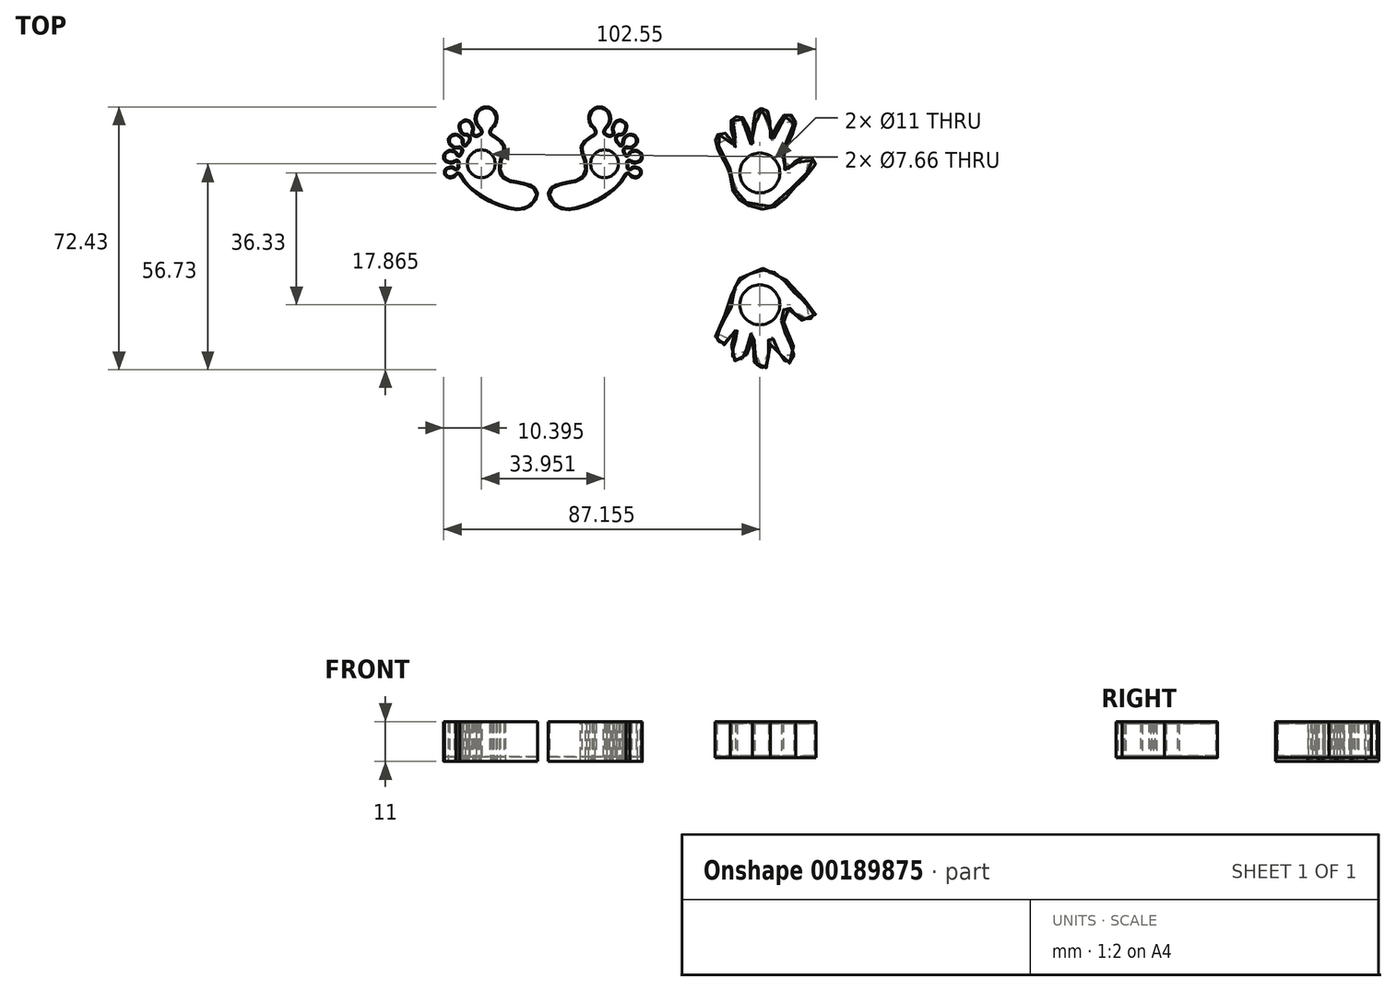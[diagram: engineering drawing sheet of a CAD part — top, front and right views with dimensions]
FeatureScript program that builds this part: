
annotation { "Feature Type Name" : "Feature", "Feature Type Description" : "" }
export const myFeature = defineFeature(function(context is Context, id is Id, definition is map)
    precondition{}
    {
        {
            var Q0;
            Q0=qCreatedBy(makeId("Top.planeOp"),FACE);
            var sketch = newSketch(context, id + "F0", { "sketchPlane" : qUnion([Q0])});
            skFitSpline(sketch, "E0", {"points": [v(-38.1, 15.91) * mm, v(-41.17, 17.42) * mm, v(-41.33, 22.02) * mm, v(-40.43, 25.18) * mm, v(-43.51, 28.42) * mm, v(-47.73, 28.72) * mm, v(-51.85, 25.13) * mm, v(-53.32, 19) * mm, v(-49.92, 13.8) * mm, v(-44.12, 10.03) * mm, v(-37.56, 8.03) * mm, v(-33.86, 8.82) * mm, v(-31.52, 11.84) * mm, v(-32.2, 13.95) * mm, v(-34.84, 15.23) * mm, v(-38.1, 15.91) * mm]});
            skFitSpline(sketch, "E1", {"points": [v(-45.64, 29.93) * mm, v(-43.87, 30.6) * mm, v(-42.7, 32.44) * mm, v(-43.04, 34.88) * mm, v(-44.75, 36.27) * mm, v(-46.72, 36.18) * mm, v(-48.3, 34.75) * mm, v(-48.65, 32.6) * mm, v(-47.95, 31) * mm, v(-46.78, 30.06) * mm, v(-45.64, 29.93) * mm]});
            skFitSpline(sketch, "E2", {"points": [v(-49.41, 31.45) * mm, v(-49.98, 32.28) * mm, v(-50.87, 32.78) * mm, v(-52.04, 32.53) * mm, v(-53.03, 31.7) * mm, v(-53.06, 30.34) * mm, v(-52.61, 29.27) * mm, v(-51.97, 28.76) * mm, v(-50.65, 28.57) * mm, v(-49.57, 29.17) * mm, v(-49.03, 30.34) * mm, v(-49.41, 31.45) * mm]});
            skFitSpline(sketch, "E3", {"points": [v(-51.97, 27.04) * mm, v(-52.6, 28.18) * mm, v(-53.97, 28.89) * mm, v(-55.6, 28.32) * mm, v(-56.07, 27.05) * mm, v(-55.62, 25.97) * mm, v(-54.67, 25.18) * mm, v(-53.54, 24.99) * mm, v(-52.33, 25.56) * mm, v(-51.97, 27.04) * mm]});
            skPoint(sketch, "E4.4.internal.snap0", {"position": v(-57.36, 23.03) * mm});
            skFitSpline(sketch, "E4", {"points": [v(-57.36, 22.44) * mm, v(-57.08, 23.61) * mm, v(-55.76, 24.4) * mm, v(-54.02, 24.04) * mm, v(-53.54, 23.03) * mm, v(-54.02, 21.44) * mm, v(-55.3, 20.87) * mm, v(-56.48, 21.16) * mm, v(-57.09, 21.62) * mm, v(-57.36, 22.44) * mm]});
            skFitSpline(sketch, "E5", {"points": [v(-54.25, 19.45) * mm, v(-53.88, 19.13) * mm, v(-53.66, 18.32) * mm, v(-54.2, 17.29) * mm, v(-55.58, 16.82) * mm, v(-56.56, 17.2) * mm, v(-57.15, 18.02) * mm, v(-56.88, 19.21) * mm, v(-55.9, 19.75) * mm, v(-54.82, 19.77) * mm, v(-54.25, 19.45) * mm]});
            skFitSpline(sketch, "E6", {"points": [v(-43.51, 28.42) * mm, v(-44.4, 29.3) * mm, v(-43.87, 30.6) * mm], "startDerivative": vector(-2.53, 1.63) * mm, "endDerivative": vector(1.79, 2.7) * mm});
            skFitSpline(sketch, "E7", {"points": [v(-47.73, 28.72) * mm, v(-47, 29.35) * mm, v(-47.41, 30.46) * mm], "startDerivative": vector(2.09, 1.14) * mm, "endDerivative": vector(-1.38, 2.3) * mm});
            skFitSpline(sketch, "E8", {"points": [v(-48.22, 28.52) * mm, v(-49.15, 28.79) * mm, v(-49.22, 29.66) * mm], "startDerivative": vector(-2.81, -0.03) * mm, "endDerivative": vector(0.87, 2.36) * mm});
            skFitSpline(sketch, "E9", {"points": [v(-50.47, 26.88) * mm, v(-50.35, 28.04) * mm, v(-50.96, 28.55) * mm], "startDerivative": vector(1.15, 2.94) * mm, "endDerivative": vector(-2.3, 0.33) * mm});
            skFitSpline(sketch, "E10", {"points": [v(-51.28, 25.94) * mm, v(-51.74, 25.98) * mm, v(-51.96, 26.57) * mm], "startDerivative": vector(-1.33, -0.55) * mm, "endDerivative": vector(-0.3, 1.2) * mm});
            skFitSpline(sketch, "E11", {"points": [v(-52.37, 24.2) * mm, v(-52.56, 24.84) * mm, v(-53.07, 25.08) * mm], "startDerivative": vector(0.03, 1.48) * mm, "endDerivative": vector(-1.63, 0.12) * mm});
            skFitSpline(sketch, "E12", {"points": [v(-52.74, 23.38) * mm, v(-53.1, 23.03) * mm, v(-53.61, 23.47) * mm], "startDerivative": vector(-0.84, -1.47) * mm, "endDerivative": vector(-0.87, 1.67) * mm});
            skFitSpline(sketch, "E13", {"points": [v(-53.38, 20.87) * mm, v(-53.54, 21.35) * mm, v(-54.25, 21.22) * mm], "startDerivative": vector(0.22, 1.99) * mm, "endDerivative": vector(-1.97, -1.2) * mm});
            skFitSpline(sketch, "E14", {"points": [v(-52.87, 17.57) * mm, v(-53.3, 17.9) * mm, v(-53.9, 17.63) * mm], "startDerivative": vector(-0.86, 1) * mm, "endDerivative": vector(-1.18, -0.85) * mm});
            skFitSpline(sketch, "E15", {"points": [v(-53.41, 19.75) * mm, v(-53.66, 19.44) * mm, v(-54.16, 19.39) * mm], "startDerivative": vector(-0.37, -1.42) * mm, "endDerivative": vector(-1.16, 0.72) * mm});
            skSolve(sketch);
        }
        {
            var Q0;
            Q0 = qSketchRegion(id + "F0", true);
            extrude(context, id + "F1", {"entities" : qUnion([Q0]), "depth" : 10 * mm});
        }
        {
            var Q0;
            Q0=makeQuery(id+"F1.opExtrude","CAP_FACE",FACE,{"disambiguationData":[OSD([sQuery(id+"F0.wireOp",EDGE,"E0"),sQuery(id+"F0.wireOp",EDGE,"E1"),sQuery(id+"F0.wireOp",EDGE,"E2"),sQuery(id+"F0.wireOp",EDGE,"E3"),sQuery(id+"F0.wireOp",EDGE,"E4"),sQuery(id+"F0.wireOp",EDGE,"E5"),sQuery(id+"F0.wireOp",EDGE,"E6"),sQuery(id+"F0.wireOp",EDGE,"E7"),sQuery(id+"F0.wireOp",EDGE,"E8"),sQuery(id+"F0.wireOp",EDGE,"E9"),sQuery(id+"F0.wireOp",EDGE,"E0"),sQuery(id+"F0.wireOp",EDGE,"E10"),sQuery(id+"F0.wireOp",EDGE,"E11"),sQuery(id+"F0.wireOp",EDGE,"E12"),sQuery(id+"F0.wireOp",EDGE,"E13"),sQuery(id+"F0.wireOp",EDGE,"E14"),sQuery(id+"F0.wireOp",EDGE,"E15"),sQuery(id+"F0.wireOp",EDGE,"E0"),sQuery(id+"F0.wireOp",EDGE,"E0"),sQuery(id+"F0.wireOp",EDGE,"E0")])],"isStart":false});
            shell(context, id + "F2", {"entities" : qUnion([Q0]), "thickness" : .3 * mm});
        }
        {
            var Q0;
            {var subQ0=sQuery(id+"F0.wireOp",EDGE,"E1");Q0=makeQuery(id+"F2.opShell","OFFSET_EDGE",EDGE,{"disambiguationData":[OSD([subQ0]),TDD([makeQuery(id+"F1.opExtrude","CAP_EDGE",EDGE,{"disambiguationData":[OSD([subQ0])],"isStart":false})])]});}
            var Q1;
            {var subQ0=sQuery(id+"F0.wireOp",EDGE,"E2");Q1=makeQuery(id+"F2.opShell","OFFSET_EDGE",EDGE,{"disambiguationData":[OSD([subQ0]),TDD([makeQuery(id+"F1.opExtrude","CAP_EDGE",EDGE,{"disambiguationData":[OSD([subQ0])],"isStart":false})])]});}
            var Q2;
            {var subQ0=sQuery(id+"F0.wireOp",EDGE,"E3");Q2=makeQuery(id+"F2.opShell","OFFSET_EDGE",EDGE,{"disambiguationData":[OSD([subQ0]),TDD([makeQuery(id+"F1.opExtrude","CAP_EDGE",EDGE,{"disambiguationData":[OSD([subQ0])],"isStart":false})])]});}
            var Q3;
            {var subQ0=sQuery(id+"F0.wireOp",EDGE,"E4");Q3=makeQuery(id+"F2.opShell","OFFSET_EDGE",EDGE,{"disambiguationData":[OSD([subQ0]),TDD([makeQuery(id+"F1.opExtrude","CAP_EDGE",EDGE,{"disambiguationData":[OSD([subQ0])],"isStart":false})])]});}
            var Q4;
            {var subQ0=sQuery(id+"F0.wireOp",EDGE,"E5");Q4=makeQuery(id+"F2.opShell","OFFSET_EDGE",EDGE,{"disambiguationData":[OSD([subQ0]),TDD([makeQuery(id+"F1.opExtrude","CAP_EDGE",EDGE,{"disambiguationData":[OSD([subQ0])],"isStart":false})])]});}
            var Q5;
            {var subQ0=sQuery(id+"F0.wireOp",EDGE,"E7");Q5=makeQuery(id+"F2.opShell","OFFSET_EDGE",EDGE,{"disambiguationData":[OSD([subQ0]),TDD([makeQuery(id+"F1.opExtrude","CAP_EDGE",EDGE,{"disambiguationData":[OSD([subQ0])],"isStart":false})])]});}
            var Q6;
            {var subQ0=sQuery(id+"F0.wireOp",EDGE,"E8");Q6=makeQuery(id+"F2.opShell","OFFSET_EDGE",EDGE,{"disambiguationData":[OSD([subQ0]),TDD([makeQuery(id+"F1.opExtrude","CAP_EDGE",EDGE,{"disambiguationData":[OSD([subQ0])],"isStart":false})])]});}
            var Q7;
            {var subQ0=sQuery(id+"F0.wireOp",EDGE,"E9");Q7=makeQuery(id+"F2.opShell","OFFSET_EDGE",EDGE,{"disambiguationData":[OSD([subQ0]),TDD([makeQuery(id+"F1.opExtrude","CAP_EDGE",EDGE,{"disambiguationData":[OSD([subQ0])],"isStart":false})])]});}
            var Q8;
            {var subQ0=sQuery(id+"F0.wireOp",EDGE,"E10");Q8=makeQuery(id+"F2.opShell","OFFSET_EDGE",EDGE,{"disambiguationData":[OSD([subQ0]),TDD([makeQuery(id+"F1.opExtrude","CAP_EDGE",EDGE,{"disambiguationData":[OSD([subQ0])],"isStart":false})])]});}
            var Q9;
            {var subQ0=sQuery(id+"F0.wireOp",EDGE,"E11");Q9=makeQuery(id+"F2.opShell","OFFSET_EDGE",EDGE,{"disambiguationData":[OSD([subQ0]),TDD([makeQuery(id+"F1.opExtrude","CAP_EDGE",EDGE,{"disambiguationData":[OSD([subQ0])],"isStart":false})])]});}
            var Q10;
            {var subQ0=sQuery(id+"F0.wireOp",EDGE,"E12");Q10=makeQuery(id+"F2.opShell","OFFSET_EDGE",EDGE,{"disambiguationData":[OSD([subQ0]),TDD([makeQuery(id+"F1.opExtrude","CAP_EDGE",EDGE,{"disambiguationData":[OSD([subQ0])],"isStart":false})])]});}
            var Q11;
            {var subQ0=sQuery(id+"F0.wireOp",EDGE,"E13");Q11=makeQuery(id+"F2.opShell","OFFSET_EDGE",EDGE,{"disambiguationData":[OSD([subQ0]),TDD([makeQuery(id+"F1.opExtrude","CAP_EDGE",EDGE,{"disambiguationData":[OSD([subQ0])],"isStart":false})])]});}
            var Q12;
            {var subQ0=sQuery(id+"F0.wireOp",EDGE,"E15");Q12=makeQuery(id+"F2.opShell","OFFSET_EDGE",EDGE,{"disambiguationData":[OSD([subQ0]),TDD([makeQuery(id+"F1.opExtrude","CAP_EDGE",EDGE,{"disambiguationData":[OSD([subQ0])],"isStart":false})])]});}
            var Q13;
            {var subQ0=sQuery(id+"F0.wireOp",EDGE,"E14");Q13=makeQuery(id+"F2.opShell","OFFSET_EDGE",EDGE,{"disambiguationData":[OSD([subQ0]),TDD([makeQuery(id+"F1.opExtrude","CAP_EDGE",EDGE,{"disambiguationData":[OSD([subQ0])],"isStart":false})])]});}
            var Q14;
            {var subQ0=sQuery(id+"F0.wireOp",EDGE,"E0");Q14=makeQuery(id+"F2.opShell","OFFSET_EDGE",EDGE,{"disambiguationData":[OSD([subQ0]),TDD([makeQuery(id+"F1.opExtrude","CAP_EDGE",EDGE,{"disambiguationData":[OSD([subQ0])],"isStart":false})])]});}
            var Q15;
            {var subQ0=sQuery(id+"F0.wireOp",EDGE,"E6");Q15=makeQuery(id+"F2.opShell","OFFSET_EDGE",EDGE,{"disambiguationData":[OSD([subQ0]),TDD([makeQuery(id+"F1.opExtrude","CAP_EDGE",EDGE,{"disambiguationData":[OSD([subQ0])],"isStart":false})])]});}
            var Q16;
            {var subQ0=sQuery(id+"F0.wireOp",EDGE,"E0");Q16=makeQuery(id+"F2.opShell","OFFSET_EDGE",EDGE,{"disambiguationData":[OSD([subQ0]),TDD([makeQuery(id+"F1.opExtrude","CAP_EDGE",EDGE,{"disambiguationData":[OSD([subQ0])],"isStart":false})])]});}
            chamfer(context, id + "F3", {"entities" : qUnion([Q0, Q1, Q2, Q3, Q4, Q5, Q6, Q7, Q8, Q9, Q10, Q11, Q12, Q13, Q14, Q15, Q16]), "width" : .2 * mm, "tangentPropagation" : true});
        }
        {
            var Q0;
            Q0=makeQuery(id+"F1.opExtrude","CAP_FACE",FACE,{"disambiguationData":[OSD([sQuery(id+"F0.wireOp",EDGE,"E0"),sQuery(id+"F0.wireOp",EDGE,"E1"),sQuery(id+"F0.wireOp",EDGE,"E2"),sQuery(id+"F0.wireOp",EDGE,"E3"),sQuery(id+"F0.wireOp",EDGE,"E4"),sQuery(id+"F0.wireOp",EDGE,"E5"),sQuery(id+"F0.wireOp",EDGE,"E6"),sQuery(id+"F0.wireOp",EDGE,"E7"),sQuery(id+"F0.wireOp",EDGE,"E8"),sQuery(id+"F0.wireOp",EDGE,"E9"),sQuery(id+"F0.wireOp",EDGE,"E0"),sQuery(id+"F0.wireOp",EDGE,"E10"),sQuery(id+"F0.wireOp",EDGE,"E11"),sQuery(id+"F0.wireOp",EDGE,"E12"),sQuery(id+"F0.wireOp",EDGE,"E13"),sQuery(id+"F0.wireOp",EDGE,"E14"),sQuery(id+"F0.wireOp",EDGE,"E15"),sQuery(id+"F0.wireOp",EDGE,"E0"),sQuery(id+"F0.wireOp",EDGE,"E0"),sQuery(id+"F0.wireOp",EDGE,"E0")])],"isStart":true});
            var sketch = newSketch(context, id + "F4", { "sketchPlane" : qUnion([Q0])});
            skCircle(sketch, "E16", {"center": v(-46.98, -20.7) * mm, "radius": 3.83 * mm});
            skSolve(sketch);
        }
        {
            var Q0;
            Q0 = qSketchRegion(id + "F4", true);
            extrude(context, id + "F5", {"entities" : qUnion([Q0]), "operationType" : NewBodyOperationType.REMOVE, "oppositeDirection" : true, "depth" : 25 * mm});
        }
        {
            var Q0;
            Q0=makeQuery(id+"F1.opExtrude","SWEPT_BODY",BODY,{"disambiguationData":[OSD([sQuery(id+"F0.wireOp",EDGE,"E0"),sQuery(id+"F0.wireOp",EDGE,"E1"),sQuery(id+"F0.wireOp",EDGE,"E2"),sQuery(id+"F0.wireOp",EDGE,"E3"),sQuery(id+"F0.wireOp",EDGE,"E4"),sQuery(id+"F0.wireOp",EDGE,"E5"),sQuery(id+"F0.wireOp",EDGE,"E6"),sQuery(id+"F0.wireOp",EDGE,"E7"),sQuery(id+"F0.wireOp",EDGE,"E8"),sQuery(id+"F0.wireOp",EDGE,"E9"),sQuery(id+"F0.wireOp",EDGE,"E0"),sQuery(id+"F0.wireOp",EDGE,"E10"),sQuery(id+"F0.wireOp",EDGE,"E11"),sQuery(id+"F0.wireOp",EDGE,"E12"),sQuery(id+"F0.wireOp",EDGE,"E13"),sQuery(id+"F0.wireOp",EDGE,"E14"),sQuery(id+"F0.wireOp",EDGE,"E15"),sQuery(id+"F0.wireOp",EDGE,"E0"),sQuery(id+"F0.wireOp",EDGE,"E0"),sQuery(id+"F0.wireOp",EDGE,"E0")])]});
            var Q1;
            Q1=qCreatedBy(makeId("Right.planeOp"),FACE);
            mirror(context, id + "F6", {"entities" : qUnion([Q0]), "mirrorPlane" : qUnion([Q1])});
        }
        {
            var Q0;
            Q0=makeQuery(id+"F6.opPattern","COPY",BODY,{"derivedFrom":makeQuery(id+"F1.opExtrude","SWEPT_BODY",BODY,{"disambiguationData":[OSD([sQuery(id+"F0.wireOp",EDGE,"E0"),sQuery(id+"F0.wireOp",EDGE,"E1"),sQuery(id+"F0.wireOp",EDGE,"E2"),sQuery(id+"F0.wireOp",EDGE,"E3"),sQuery(id+"F0.wireOp",EDGE,"E4"),sQuery(id+"F0.wireOp",EDGE,"E5"),sQuery(id+"F0.wireOp",EDGE,"E6"),sQuery(id+"F0.wireOp",EDGE,"E7"),sQuery(id+"F0.wireOp",EDGE,"E8"),sQuery(id+"F0.wireOp",EDGE,"E9"),sQuery(id+"F0.wireOp",EDGE,"E0"),sQuery(id+"F0.wireOp",EDGE,"E10"),sQuery(id+"F0.wireOp",EDGE,"E11"),sQuery(id+"F0.wireOp",EDGE,"E12"),sQuery(id+"F0.wireOp",EDGE,"E13"),sQuery(id+"F0.wireOp",EDGE,"E14"),sQuery(id+"F0.wireOp",EDGE,"E15"),sQuery(id+"F0.wireOp",EDGE,"E0"),sQuery(id+"F0.wireOp",EDGE,"E0"),sQuery(id+"F0.wireOp",EDGE,"E0")])]}),"instanceName":"1"});
            transform(context, id + "F7", {"entities" : qUnion([Q0]), "transformType" : TransformType.TRANSLATION_3D, "dx" : -60 * mm, "dy" : 0 * mm, "dz" : 0 * mm, "makeCopy" : false});
        }
        {
            var Q0;
            Q0=makeQuery(id+"F6.opPattern","COPY",FACE,{"derivedFrom":makeQuery(id+"F1.opExtrude","CAP_FACE",FACE,{"disambiguationData":[OSD([sQuery(id+"F0.wireOp",EDGE,"E0"),sQuery(id+"F0.wireOp",EDGE,"E1"),sQuery(id+"F0.wireOp",EDGE,"E2"),sQuery(id+"F0.wireOp",EDGE,"E3"),sQuery(id+"F0.wireOp",EDGE,"E4"),sQuery(id+"F0.wireOp",EDGE,"E5"),sQuery(id+"F0.wireOp",EDGE,"E6"),sQuery(id+"F0.wireOp",EDGE,"E7"),sQuery(id+"F0.wireOp",EDGE,"E8"),sQuery(id+"F0.wireOp",EDGE,"E9"),sQuery(id+"F0.wireOp",EDGE,"E0"),sQuery(id+"F0.wireOp",EDGE,"E10"),sQuery(id+"F0.wireOp",EDGE,"E11"),sQuery(id+"F0.wireOp",EDGE,"E12"),sQuery(id+"F0.wireOp",EDGE,"E13"),sQuery(id+"F0.wireOp",EDGE,"E14"),sQuery(id+"F0.wireOp",EDGE,"E15"),sQuery(id+"F0.wireOp",EDGE,"E0"),sQuery(id+"F0.wireOp",EDGE,"E0"),sQuery(id+"F0.wireOp",EDGE,"E0")])],"isStart":true}),"instanceName":"1"});
            extrude(context, id + "F8", {"entities" : qUnion([Q0]), "operationType" : NewBodyOperationType.ADD, "depth" : 1 * mm});
        }
        {
            var Q0;
            Q0=makeQuery(id+"F1.opExtrude","CAP_FACE",FACE,{"disambiguationData":[OSD([sQuery(id+"F0.wireOp",EDGE,"E0"),sQuery(id+"F0.wireOp",EDGE,"E1"),sQuery(id+"F0.wireOp",EDGE,"E2"),sQuery(id+"F0.wireOp",EDGE,"E3"),sQuery(id+"F0.wireOp",EDGE,"E4"),sQuery(id+"F0.wireOp",EDGE,"E5"),sQuery(id+"F0.wireOp",EDGE,"E6"),sQuery(id+"F0.wireOp",EDGE,"E7"),sQuery(id+"F0.wireOp",EDGE,"E8"),sQuery(id+"F0.wireOp",EDGE,"E9"),sQuery(id+"F0.wireOp",EDGE,"E0"),sQuery(id+"F0.wireOp",EDGE,"E10"),sQuery(id+"F0.wireOp",EDGE,"E11"),sQuery(id+"F0.wireOp",EDGE,"E12"),sQuery(id+"F0.wireOp",EDGE,"E13"),sQuery(id+"F0.wireOp",EDGE,"E14"),sQuery(id+"F0.wireOp",EDGE,"E15"),sQuery(id+"F0.wireOp",EDGE,"E0"),sQuery(id+"F0.wireOp",EDGE,"E0"),sQuery(id+"F0.wireOp",EDGE,"E0")])],"isStart":true});
            extrude(context, id + "F9", {"entities" : qUnion([Q0]), "operationType" : NewBodyOperationType.ADD, "depth" : 1 * mm});
        }
        {
            var Q0;
            Q0=qCreatedBy(makeId("Top.planeOp"),FACE);
            var sketch = newSketch(context, id + "F10", { "sketchPlane" : qUnion([Q0])});
            skFitSpline(sketch, "E17", {"points": [v(30.57, 8.13) * mm, v(35.2, 9.65) * mm, v(39.52, 14.28) * mm, v(42.15, 16.84) * mm, v(44.31, 19.4) * mm, v(45.18, 20.99) * mm, v(43.93, 22.46) * mm, v(41.37, 22.48) * mm, v(39, 20.81) * mm, v(37.73, 19.41) * mm, v(37.33, 19.12) * mm, v(36.46, 20.34) * mm, v(36.53, 23.81) * mm, v(38.52, 28.42) * mm, v(39.56, 32.35) * mm, v(38.33, 34.15) * mm, v(36.59, 34.15) * mm, v(34.53, 31.33) * mm, v(32.62, 27.02) * mm, v(32.63, 27.32) * mm, v(32.42, 33.93) * mm, v(31.63, 35.45) * mm, v(30.3, 36.03) * mm, v(28.72, 35.25) * mm, v(28.04, 31.84) * mm, v(27.78, 27.18) * mm, v(27.84, 26.22) * mm, v(25.84, 32.57) * mm, v(24.76, 33.59) * mm, v(23.35, 33.76) * mm, v(22.22, 33.16) * mm, v(21.63, 31.8) * mm, v(22.25, 28.73) * mm, v(22.84, 26.44) * mm, v(23.01, 25.29) * mm, v(22.62, 26.05) * mm, v(20.81, 28.82) * mm, v(18.83, 29.15) * mm, v(17.65, 28.14) * mm, v(17.5, 27.2) * mm, v(18.16, 24.84) * mm, v(20.5, 20.3) * mm, v(21.68, 17.82) * mm, v(22.01, 14.45) * mm, v(23.01, 12.17) * mm, v(25.53, 9.84) * mm, v(30.57, 8.13) * mm]});
            skSolve(sketch);
        }
        {
            var Q0;
            Q0 = qSketchRegion(id + "F10", true);
            extrude(context, id + "F11", {"entities" : qUnion([Q0]), "depth" : 10 * mm});
        }
        {
            var Q0;
            Q0=makeQuery(id+"F11.opExtrude","CAP_FACE",FACE,{"disambiguationData":[OSD([sQuery(id+"F10.wireOp",EDGE,"E17")])],"isStart":false});
            shell(context, id + "F12", {"entities" : qUnion([Q0]), "thickness" : .5 * mm});
        }
        {
            var Q0;
            {var subQ0=sQuery(id+"F10.wireOp",EDGE,"E17");Q0=makeQuery(id+"F12.opShell","OFFSET_EDGE",EDGE,{"disambiguationData":[OSD([subQ0]),TDD([makeQuery(id+"F11.opExtrude","CAP_EDGE",EDGE,{"disambiguationData":[OSD([subQ0])],"isStart":false})])]});}
            chamfer(context, id + "F13", {"entities" : qUnion([Q0]), "width" : 0.5 * mm, "tangentPropagation" : true});
        }
        {
            var Q0;
            Q0=makeQuery(id+"F11.opExtrude","CAP_FACE",FACE,{"disambiguationData":[OSD([sQuery(id+"F10.wireOp",EDGE,"E17")])],"isStart":true});
            var sketch = newSketch(context, id + "F14", { "sketchPlane" : qUnion([Q0])});
            skCircle(sketch, "E18", {"center": v(29.79, -18.17) * mm, "radius": 5.5 * mm});
            skSolve(sketch);
        }
        {
            var Q0;
            Q0 = qSketchRegion(id + "F14", true);
            extrude(context, id + "F15", {"entities" : qUnion([Q0]), "operationType" : NewBodyOperationType.REMOVE, "oppositeDirection" : true, "depth" : 25 * mm});
        }
        {
            var Q0;
            Q0=makeQuery(id+"F11.opExtrude","SWEPT_BODY",BODY,{"disambiguationData":[OSD([sQuery(id+"F10.wireOp",EDGE,"E17")])]});
            var Q1;
            Q1=qCreatedBy(makeId("Front.planeOp"),FACE);
            mirror(context, id + "F16", {"entities" : qUnion([Q0]), "mirrorPlane" : qUnion([Q1])});
        }
    });
